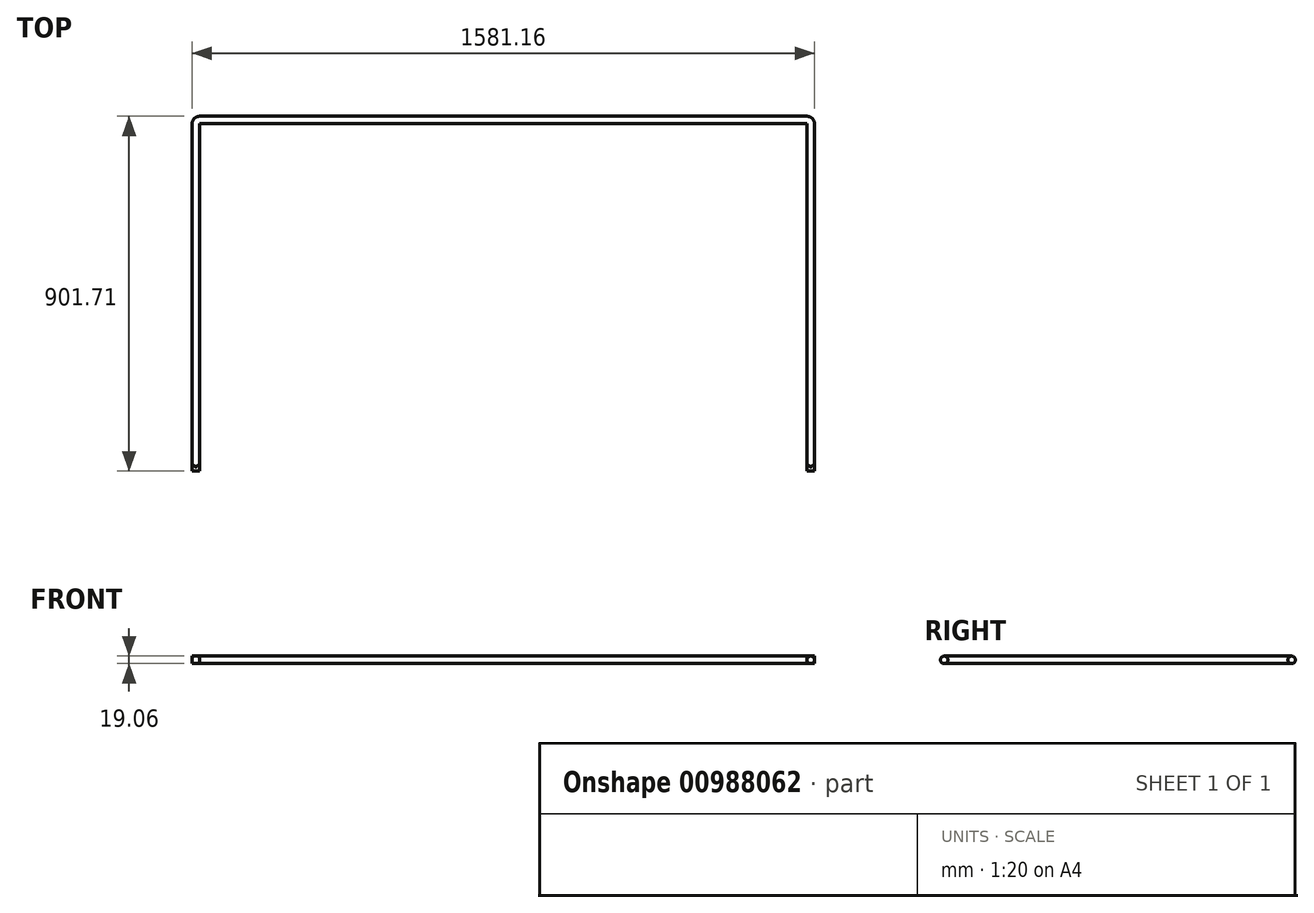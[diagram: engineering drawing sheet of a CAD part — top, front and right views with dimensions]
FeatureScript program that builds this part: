
annotation { "Feature Type Name" : "Feature", "Feature Type Description" : "" }
export const myFeature = defineFeature(function(context is Context, id is Id, definition is map)
    precondition{}
    {
        {
            var Q0;
            Q0=qCreatedBy(makeId("Top.planeOp"),FACE);
            var sketch = newSketch(context, id + "F0", { "sketchPlane" : qUnion([Q0])});
            skLineSegment(sketch, "E0", {"start": v(0, 0) * mm, "end": v(0, 873.12) * mm});
            skLineSegment(sketch, "E1", {"start": v(9.53, 882.65) * mm, "end": v(1552.58, 882.65) * mm});
            skLineSegment(sketch, "E2", {"start": v(1562.1, 873.12) * mm, "end": v(1562.1, 0) * mm});
            skPoint(sketch, "E3.visualSharp", {"position": v(0, 882.65) * mm});
            skPoint(sketch, "E4.visualSharp", {"position": v(1562.1, 882.65) * mm});
            skArc(sketch, "E5.filletArc", {"start": v(9.53, 882.65) * mm, "mid": v(2.79, 879.86) * mm, "end": v(0, 873.12) * mm});
            skArc(sketch, "E6.filletArc", {"start": v(1562.1, 873.12) * mm, "mid": v(1559.31, 879.86) * mm, "end": v(1552.58, 882.65) * mm});
            skSolve(sketch);
        }
        {
            var Q0;
            Q0=qCreatedBy(makeId("Front.planeOp"),FACE);
            var sketch = newSketch(context, id + "F1", { "sketchPlane" : qUnion([Q0])});
            skCircle(sketch, "E7", {"center": v(0, 0) * mm, "radius": 9.53 * mm});
            skSolve(sketch);
        }
        {
            var Q0;
            Q0 = qSketchRegion(id + "F1", true);
            var Q1;
            Q1 = qConstructionFilter(qBodyType(qCreatedBy(id + "F0" ,EDGE), BodyType.WIRE), ConstructionObject.NO);
            sweep(context, id + "F2", {"profiles" : qUnion([Q0]), "path" : qUnion([Q1])});
        }
        {
            var Q0;
            Q0=qCreatedBy(makeId("Right.planeOp"),FACE);
            var sketch = newSketch(context, id + "F3", { "sketchPlane" : qUnion([Q0])});
            skCircle(sketch, "E8", {"center": v(0, 0) * mm, "radius": 9.52 * mm});
            skSolve(sketch);
        }
        {
            var Q0;
            Q0 = qSketchRegion(id + "F3", true);
            extrude(context, id + "F4", {"entities" : qUnion([Q0]), "operationType" : NewBodyOperationType.ADD, "endBound" : BoundingType.SYMMETRIC, "depth" : 19.05 * mm, "offsetDistance" : 25.4 * mm});
        }
        {
            var Q0;
            Q0=qCreatedBy(makeId("Right.planeOp"),FACE);
            cPlane(context, id + "F5", {"entities" : qUnion([Q0]), "cplaneType" : CPlaneType.OFFSET, "offset" : 1562.1 * mm, "width" : 152.4 * mm, "height" : 152.4 * mm});
        }
        {
            var Q0;
            Q0=qCreatedBy(id+"F5.planeOp",FACE);
            var sketch = newSketch(context, id + "F6", { "sketchPlane" : qUnion([Q0])});
            skCircle(sketch, "E9", {"center": v(0, 0) * mm, "radius": 9.53 * mm});
            skSolve(sketch);
        }
        {
            var Q0;
            Q0 = qSketchRegion(id + "F6", true);
            extrude(context, id + "F7", {"entities" : qUnion([Q0]), "operationType" : NewBodyOperationType.ADD, "endBound" : BoundingType.SYMMETRIC, "depth" : 19.05 * mm, "offsetDistance" : 25.4 * mm});
        }
    });
